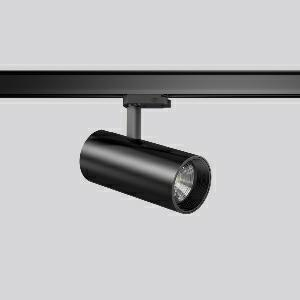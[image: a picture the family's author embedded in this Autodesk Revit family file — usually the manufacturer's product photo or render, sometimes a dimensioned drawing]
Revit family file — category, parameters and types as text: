
# Revit family: deecos_s_mini_742208_003_1e4b
name_source: partatom
category: Lighting Fixtures
units: mm (PartAtom-declared; Revit-internal decimal feet)

## family parameters
Cut with Voids When Loaded = No
Host = Face
Light Source = No
Part Type = Normal
Room Calculation Point = No
Round Connector Dimension = Use Diameter
Shared = No

## types (1)
- DEECOS S mini (1 x LED Modul 930, 2850 lm, 3000)
    Apparent Load = 29 VA
    Approval mark = CE
    CIE Flux Codes = 98 100 100 100 100
    Color Rendering = 90
    Color Temperature = 3000
    Default Elevation = 1800 mm
    Description = Series: DEECOS S mini
LED surface-mounted projector in modern design with no visible cooling ribs. Housing: die-cast aluminium, powder-coated. Rotation range: 356°. Swivel range: 90°. Black plastic ring and recessed LED to prevent glare from the side. Optical assembly with lens made of plastic (polycarbonate) for the best homogeneous light distribution - can be changed without tools. Best colour rendering index Ra>90. With multi adaptor for 3-circuit tracks 230 V. Suitable for Track on ceiling, Wall track. High quality converter without flickering and stroboscopic effect. The following accessories can be mounted without use of tools: interchangeable lenses, decorative glasses, honeycomb louvre, clear and frosted diffusers, white interchangeable plastic ring. 
Colour: deep black, matt (RAL 9005)
Diameter: 87 mm
Height: 214 mm
Lamp: LED
Socket: without socket
Colour temperature: 3000K
Colour rendering index (CRI): 92
System power: 29 W
Rated luminous flux: 2850 lm
Luminous efficiency: 98 lm/W
Control gear: Regulated power supply
Protection class: I
Type of protection: IP 20
    Height = 214 mm
    Lamp = 1 x LED Modul 930
    Lamp Light Flux = 2850 lm
    Lamp count = 1
    Length = 87 mm
    Lifetime = 50000 h
    Luminous efficacy = 98 lm/W
    Manufacturer = RZB
    ModVariant = No
    Model = 742208.003
    Mounting Place = Ceiling
    Mounting Type = Rail mounted
    Number of Poles = 1
    OnlyDefault = Yes
    Power Factor = 1
    Product Name = DEECOS S mini
    Product group = Track mounted projectors
    ProductGroupID = 301
    Protection Class = Protection class I
    Protection Degree = IP 20
    RLX_Detail_Level = 1
    RLX_Emergency_Light_Flux = 0 lm
    RLX_Emergency_Type = 0
    RLX_Emergency_Type_DB = No
    RlxData = <blob elided: 38669 chars, md5=952c8971>
    Socket = socket
    Standby Power = 0 W
    System Light Flux = 2850 lm
    System Power = 29 W
    Type Comments = Product without accessories
    Type Image = 741930.003.jpg
    URL = http://relux.com
    VarID = ---
    Voltage = 230 V
    Voltage Range = 220-240 V
    Weight = 0.00 kg
    Width = 0 mm  [stored 0 ft]

note: [stored X ft] marks values corroborated as IEEE doubles in the binary element streams (Revit-internal decimal feet)

## geometry (parser evidence)
native form markers: Blend x4, Sweep x11
no freeform markers — native parametric forms only
